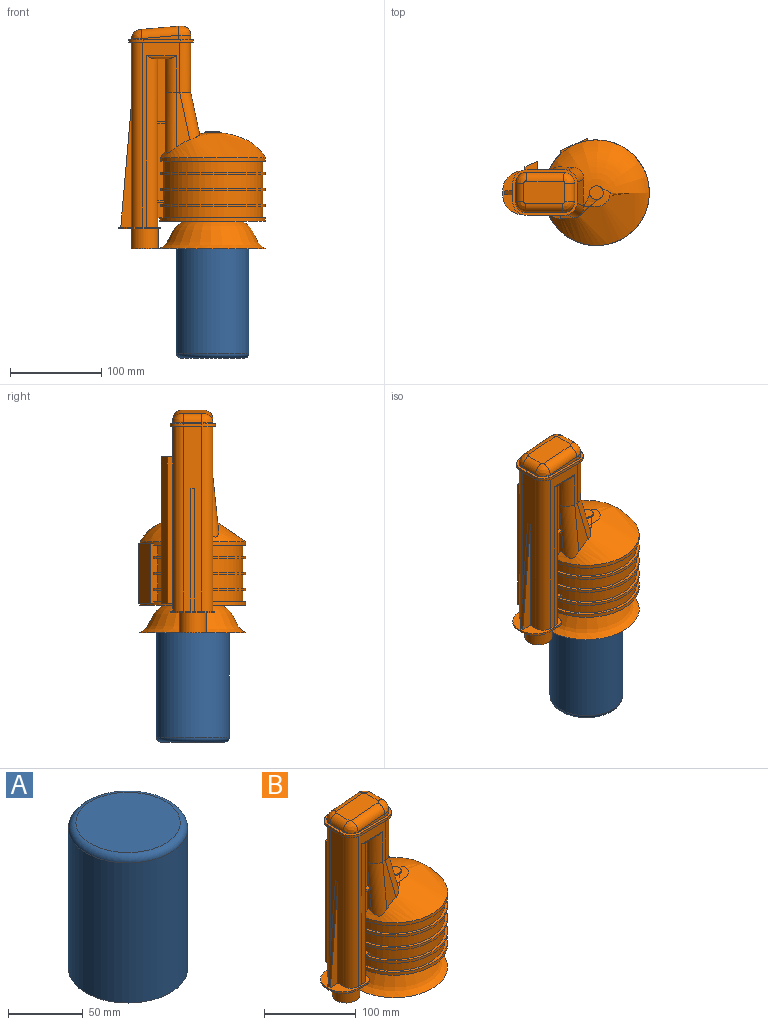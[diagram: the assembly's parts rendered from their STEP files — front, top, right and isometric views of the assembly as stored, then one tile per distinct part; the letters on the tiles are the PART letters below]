
ASSEMBLY  parts=2 mates=1
PART A: 4 faces, bbox 86.6x86.6x120 mm
  f0: cylinder r=40mm len=115mm, axis (0,0,-1), area 28902.7mm2, adj f2,f3
  f1: plane 70x70mm, normal (0,0,1), area 3848.5mm2, adj f3
  f2: plane 80x80mm, normal (0,0,-1), area 5026.5mm2, adj f0
  f3: torus R=35mm, axis (0,0,1), area 1884.3mm2, adj f0,f1
PART B: 131 faces, bbox 163.3x120x248 mm
  f0: plane 8.21x5mm, normal (0,1,0), area 41mm2, adj f1,f33,f103,f129
  f1: cylinder r=12mm len=188mm, axis (0,0,-1), area 2199.6mm2, adj f0,f28,f29,f31,f33,f55,f89,f127
  f2: cylinder r=55mm len=110mm, axis (0,0,1), area 3112.4mm2, adj f5,f7,f32,f123
  f3: cylinder r=55mm len=110mm, axis (0,0,1), area 3750.6mm2, adj f11,f30,f32,f36,f91,f92,f93,f123
  f4: plane 32.65x17.83mm, normal (0,0,1), area 105.4mm2, adj f12,f29,f34,f122
  f5: plane 116x115.13mm, normal (0,0,1), area 799.3mm2, adj f2,f12,f32,f123
  f6: plane 32.65x17.83mm, normal (0,0,-1), area 105.4mm2, adj f8,f29,f34,f122
  f7: plane 116x115.13mm, normal (0,0,-1), area 799.3mm2, adj f2,f9,f32,f123
  f8: cylinder r=58mm len=32.65mm, axis (0,0,1), area 113.6mm2, adj f6,f10,f29,f122
  f9: cylinder r=58mm len=116mm, axis (0,0,1), area 820.5mm2, adj f7,f11,f32,f123
  f10: plane 32.65x17.83mm, normal (0,0,1), area 105.4mm2, adj f8,f29,f35,f122
  f11: plane 116x115.13mm, normal (0,0,1), area 799.3mm2, adj f3,f9,f32,f123
  f12: cylinder r=58mm len=116mm, axis (0,0,1), area 1389.3mm2, adj f4,f5,f47,f49,f122,f123,f128
  f13: plane 32.65x17.83mm, normal (0,0,-1), area 105.4mm2, adj f14,f29,f35,f122
  f14: cylinder r=58mm len=32.65mm, axis (0,0,1), area 113.6mm2, adj f13,f15,f29,f122
  f15: plane 32.65x17.83mm, normal (0,0,1), area 105.4mm2, adj f14,f16,f29,f122
  f16: cylinder r=55mm len=28.36mm, axis (0,0,1), area 469.8mm2, adj f15,f17,f29,f122
  f17: plane 32.65x17.83mm, normal (0,0,-1), area 105.4mm2, adj f16,f18,f29,f122
  f18: cylinder r=58mm len=32.65mm, axis (0,0,1), area 113.6mm2, adj f17,f19,f29,f122
  f19: plane 32.65x17.83mm, normal (0,0,1), area 105.4mm2, adj f18,f20,f29,f122
  f20: cylinder r=55mm len=28.36mm, axis (0,0,1), area 388.8mm2, adj f19,f21,f29,f122
  f21: plane 32.65x17.83mm, normal (0,0,-1), area 105.4mm2, adj f20,f29,f45,f122
  f22: revolved ~116x116mm, area 10731.7mm2, adj f29,f30,f45,f50,f51,f52,f94,f96
  f23: plane 28.74x6.6mm, normal (-1,0,0), area 139mm2, adj f26,f30,f96,f100
  f24: plane 16.13x9mm, normal (0,0,-1), area 94.4mm2, adj f25,f88,f101,f102
  f25: plane 69.46x8mm, normal (0,-1,0), area 555.7mm2, adj f24,f27,f97,f101,f102
  f26: plane 9.18x5mm, normal (0,0,-1), area 41.8mm2, adj f23,f30,f90,f100,f102
  f27: plane 9.21x5mm, normal (0,0,1), area 41.8mm2, adj f25,f90,f97,f100,f102
  f28: plane 16.13x9mm, normal (0,0,-1), area 94.4mm2, adj f1,f29,f89,f98
  f29: plane 175.07x11.36mm, normal (0,1,0), area 1205.7mm2, adj f1,f4,f6,f8,f10,f13,f14,f15
  f30: plane 84.45x11.36mm, normal (0,-1,0), area 529.9mm2, adj f3,f22,f23,f26,f36,f37,f38,f39
  f31: plane 20x10.28mm, normal (1,0,0), area 205.7mm2, adj f1,f33,f49,f102
  f32: plane 17.16x5.92mm, normal (0,-1,0), area 92.4mm2, adj f2,f3,f5,f7,f9,f11,f49,f91
  f33: plane 48x46mm, normal (0,0,1), area 758.2mm2, adj f0,f1,f31,f53,f56,f57,f58,f59
  f34: cylinder r=55mm len=28.36mm, axis (0,0,1), area 388.8mm2, adj f4,f6,f29,f122
  f35: cylinder r=55mm len=28.36mm, axis (0,0,1), area 469.8mm2, adj f10,f13,f29,f122
  f36: plane 116x115.13mm, normal (0,0,-1), area 799.3mm2, adj f3,f30,f37,f123
  f37: cylinder r=58mm len=116mm, axis (0,0,1), area 820.5mm2, adj f30,f36,f38,f123
  f38: plane 116x115.13mm, normal (0,0,1), area 799.3mm2, adj f30,f37,f39,f123
  f39: cylinder r=55mm len=110mm, axis (0,0,1), area 3760.8mm2, adj f30,f38,f40,f123
  f40: plane 116x115.13mm, normal (0,0,-1), area 799.3mm2, adj f30,f39,f41,f123
  f41: cylinder r=58mm len=116mm, axis (0,0,1), area 820.5mm2, adj f30,f40,f42,f123
  f42: plane 116x115.13mm, normal (0,0,1), area 799.3mm2, adj f30,f41,f43,f123
  f43: cylinder r=55mm len=110mm, axis (0,0,1), area 3112.4mm2, adj f30,f42,f44,f123
  f44: plane 116x115.13mm, normal (0,0,-1), area 799.3mm2, adj f30,f43,f45,f123
  f45: cylinder r=58mm len=116mm, axis (0,0,1), area 1313.9mm2, adj f21,f22,f29,f30,f44,f122,f123,f124
  f46: revolved ~116x116mm, area 11430mm2, adj f47,f48
  f47: plane 116x116mm, normal (0,0,-1), area 7147.1mm2, adj f12,f46
  f48: plane 116x116mm, normal (0,0,-1), area 10568.3mm2, adj f46
  f49: plane 20x2.87mm, normal (0,0,-1), area 45.8mm2, adj f12,f29,f31,f32
  f50: plane 62.78x17.43mm, normal (0,-0.99,0.1), area 555.4mm2, adj f22,f53,f100,f105
  f51: plane 62.77x17.42mm, normal (0,0.99,0.1), area 555.4mm2, adj f22,f55,f99,f107
  f52: plane 46.46x30.17mm, normal (0.98,0,0.21), area 1174.9mm2, adj f22,f54,f105,f106,f107,f108
  f53: plane 203x41mm, normal (0,-1,0), area 1715mm2, adj f33,f50,f69,f88,f101,f102,f104,f105
  f54: plane 55x20mm, normal (1,0,0), area 1100mm2, adj f52,f69,f106,f108
  f55: plane 55x41mm, normal (0,1,0), area 869mm2, adj f1,f51,f69,f89,f98,f103,f107,f108
  f56: plane 203x20mm, normal (-1,0,0), area 3520.2mm2, adj f33,f64,f65,f66,f69,f103,f104
  f57: plane 14x2mm, normal (0,-1,0), area 28mm2, adj f33,f61,f62,f110
  f58: plane 4x2mm, normal (-1,0,0), area 8mm2, adj f33,f61,f62,f63
  f59: plane 14x2mm, normal (0,1,0), area 28mm2, adj f33,f61,f63,f109
  f60: plane 28x2mm, normal (1,0,0), area 56mm2, adj f33,f61,f109,f110
  f61: plane 48x46mm, normal (0,0,-1), area 1250.5mm2, adj f57,f58,f59,f60,f62,f63,f67,f109
  f62: cylinder r=22mm len=22mm, axis (0,0,-1), area 69.1mm2, adj f33,f57,f58,f61
  f63: cylinder r=22mm len=22mm, axis (0,0,1), area 69.1mm2, adj f33,f58,f59,f61
  f64: plane 134.95x11.7mm, normal (0,-1,0), area 789.2mm2, adj f33,f56,f66
  f65: plane 134.95x11.7mm, normal (0,1,0), area 789.2mm2, adj f33,f56,f66
  f66: plane 134.95x11.7mm, normal (-1,0,0.09), area 541.8mm2, adj f33,f56,f64,f65
  f67: cylinder r=15mm len=30mm, axis (0,0,1), area 2073.5mm2, adj f61,f68
  f68: plane 30x30mm, normal (0,0,-1), area 706.9mm2, adj f67
  f69: plane 71x50.07mm, normal (0,0,-1), area 622.5mm2, adj f53,f54,f55,f56,f70,f71,f72,f73
  f70: cylinder r=15mm len=15mm, axis (0,0,-1), area 67.8mm2, adj f69,f71,f77,f78
  f71: plane 41x3mm, normal (0,1,0), area 123mm2, adj f69,f70,f72,f78
  f72: cylinder r=15mm len=16mm, axis (0,0,-1), area 73.8mm2, adj f69,f71,f73,f78
  f73: plane 20x3mm, normal (-1,0,0), area 60mm2, adj f69,f72,f74,f78
  f74: cylinder r=15mm len=16mm, axis (0,0,-1), area 73.8mm2, adj f69,f73,f75,f78
  f75: plane 41x3mm, normal (0,-1,0), area 123mm2, adj f69,f74,f76,f78
  f76: cylinder r=15mm len=15mm, axis (0,0,-1), area 67.8mm2, adj f69,f75,f77,f78
  f77: plane 20x3mm, normal (1,0,0), area 60mm2, adj f69,f70,f76,f78
  f78: plane 71x50.07mm, normal (0,0,1), area 620.9mm2, adj f70,f71,f72,f73,f74,f75,f76,f77
  f79: plane 20.01x4.77mm, normal (1,0,0), area 95.5mm2, adj f78,f80,f86,f118
  f80: cylinder r=12mm len=12mm, axis (0,0,-1), area 84.4mm2, adj f78,f79,f81,f117
  f81: plane 41x4.68mm, normal (0,1,0), area 118.2mm2, adj f78,f80,f82,f113,f115,f117
  f82: cylinder r=12mm len=12.89mm, axis (0,0,-1), area 18.4mm2, adj f78,f81,f83,f113
  f83: plane 20.01x0.84mm, normal (-1,0,0), area 16.7mm2, adj f78,f82,f84,f111
  f84: cylinder r=12mm len=12mm, axis (0,0,-1), area 16.1mm2, adj f78,f83,f85,f112,f114
  f85: plane 41x4.52mm, normal (0,-1,0), area 111.8mm2, adj f78,f84,f86,f114
  f86: cylinder r=12mm len=12.9mm, axis (0,0,-1), area 93mm2, adj f78,f79,f85,f114,f116
  f87: plane 45x24.07mm, normal (-0.09,0,1), area 1080.9mm2, adj f111,f112,f113,f114,f115,f116,f117,f118
  f88: cylinder r=3mm len=32mm, axis (1,0,0), area 113.4mm2, adj f24,f53,f101,f102
  f89: cylinder r=3mm len=32mm, axis (-1,0,0), area 113.4mm2, adj f1,f28,f55,f98
  f90: plane 9.21x2mm, normal (0,-1,0), area 18.4mm2, adj f26,f27,f100,f102
  f91: plane 8.18x5mm, normal (0,0,-1), area 34.1mm2, adj f3,f32,f93,f102
  f92: plane 8.18x5mm, normal (0,0,1), area 34.1mm2, adj f3,f30,f93,f102
  f93: plane 8.18x2mm, normal (0,-1,0), area 16.4mm2, adj f3,f91,f92,f102
  f94: extruded ~14.97x5.76mm, area 34.4mm2, adj f22,f29,f95,f99
  f95: plane 62.57x6.6mm, normal (-1,0,0), area 199.1mm2, adj f29,f94,f99
  f96: extruded ~14.97x5.76mm, area 34.4mm2, adj f22,f23,f30,f100
  f97: plane 31.83x3.35mm, normal (-1,0,0), area 53.2mm2, adj f25,f27,f100
  f98: cylinder r=12mm len=40.63mm, axis (0,0,-1), area 716.4mm2, adj f28,f29,f55,f89,f99
  f99: cylinder r=12mm len=68.61mm, axis (0,-0.1,0.99), area 1217.6mm2, adj f22,f51,f94,f95,f98
  f100: cylinder r=12mm len=68.61mm, axis (0,0.1,0.99), area 1214.5mm2, adj f22,f23,f26,f27,f50,f90,f96,f97
  f101: cylinder r=12mm len=40.63mm, axis (0,0,1), area 716.4mm2, adj f24,f25,f53,f88,f100
  f102: cylinder r=12mm len=188mm, axis (0,0,1), area 3479.5mm2, adj f24,f25,f26,f27,f30,f31,f32,f33
  f103: cylinder r=12mm len=203mm, axis (0,0,-1), area 3579.7mm2, adj f0,f33,f55,f56,f69,f126,f129,f130
  f104: cylinder r=12mm len=203mm, axis (0,0,1), area 3826.5mm2, adj f33,f53,f56,f69
  f105: cylinder r=12mm len=53.74mm, axis (0.21,-0.1,-0.97), area 940.4mm2, adj f22,f50,f52,f53,f106
  f106: cylinder r=12mm len=55mm, axis (0,0,1), area 1033.4mm2, adj f52,f53,f54,f69,f105
  f107: cylinder r=12mm len=53.74mm, axis (0.21,0.1,-0.97), area 940.4mm2, adj f22,f51,f52,f55,f108
  f108: cylinder r=12mm len=55mm, axis (0,0,-1), area 1033.4mm2, adj f52,f54,f55,f69,f107
  f109: cylinder r=10mm len=10mm, axis (0,0,-1), area 31.4mm2, adj f33,f59,f60,f61
  f110: cylinder r=10mm len=10mm, axis (0,0,1), area 31.4mm2, adj f33,f57,f60,f61
  f111: cylinder r=10mm len=20.04mm, axis (0,1,0), area 297.1mm2, adj f83,f87,f112,f113
  f112: bspline ~12.04x11.1mm, area 181.1mm2, adj f84,f87,f111,f114
  f113: bspline ~14.18x12.07mm, area 207.9mm2, adj f81,f82,f87,f111,f115
  f114: cylinder r=10mm len=42.4mm, axis (-1,0,-0.09), area 646.5mm2, adj f84,f85,f86,f87,f112,f116
  f115: cylinder r=10mm len=42.4mm, axis (1,0,0.09), area 646.5mm2, adj f81,f87,f113,f117
  f116: bspline ~16.39x14.3mm, area 232.8mm2, adj f86,f87,f114,f118
  f117: bspline ~14.3x13.39mm, area 205.9mm2, adj f80,f81,f87,f115,f118
  f118: cylinder r=10mm len=20.04mm, axis (0,-1,0), area 332mm2, adj f79,f87,f116,f117
  f119: cylinder r=7.5mm len=15mm, axis (0,0,-1), area 74.5mm2, adj f22,f120
  f120: plane 15x15mm, normal (0,0,1), area 176.7mm2, adj f119
  f121: plane 66x29.03mm, normal (-0.42,0.91,0), area 2110.3mm2, adj f122,f123,f124,f128
  f122: plane 66x7.94mm, normal (-1,0.03,0), area 468.6mm2, adj f4,f6,f8,f10,f12,f13,f14,f15
  f123: plane 66x5.67mm, normal (1,0,0), area 334.6mm2, adj f2,f3,f5,f7,f9,f11,f12,f36
  f124: plane 29.12x17.07mm, normal (0,0,1), area 39.9mm2, adj f45,f121,f122,f123
  f125: plane 161x14.01mm, normal (-0.42,0.91,0), area 2485mm2, adj f126,f127,f129,f130
  f126: plane 161x6.23mm, normal (-1,0,0), area 1002.8mm2, adj f103,f125,f129,f130
  f127: plane 161x15.22mm, normal (1,0,0), area 2451.1mm2, adj f1,f125,f129,f130
  f128: plane 29.12x17.07mm, normal (0,0,-1), area 39.9mm2, adj f12,f121,f122,f123
  f129: plane 15.22x14.01mm, normal (0,0,-1), area 137.5mm2, adj f0,f1,f103,f125,f126,f127
  f130: plane 15.22x14.01mm, normal (0,0,1), area 137.5mm2, adj f1,f55,f103,f125,f126,f127
PLACE A rot(axis=(1,0,0),180deg) t=(68.14,-54.22,-17.82)mm
PLACE B t=(77.25,-54.22,42.1)mm
MATE fastened A.f0 <-> B.f119  axis (0,0,1) through (68.14,-54.22,-17.82)mm
